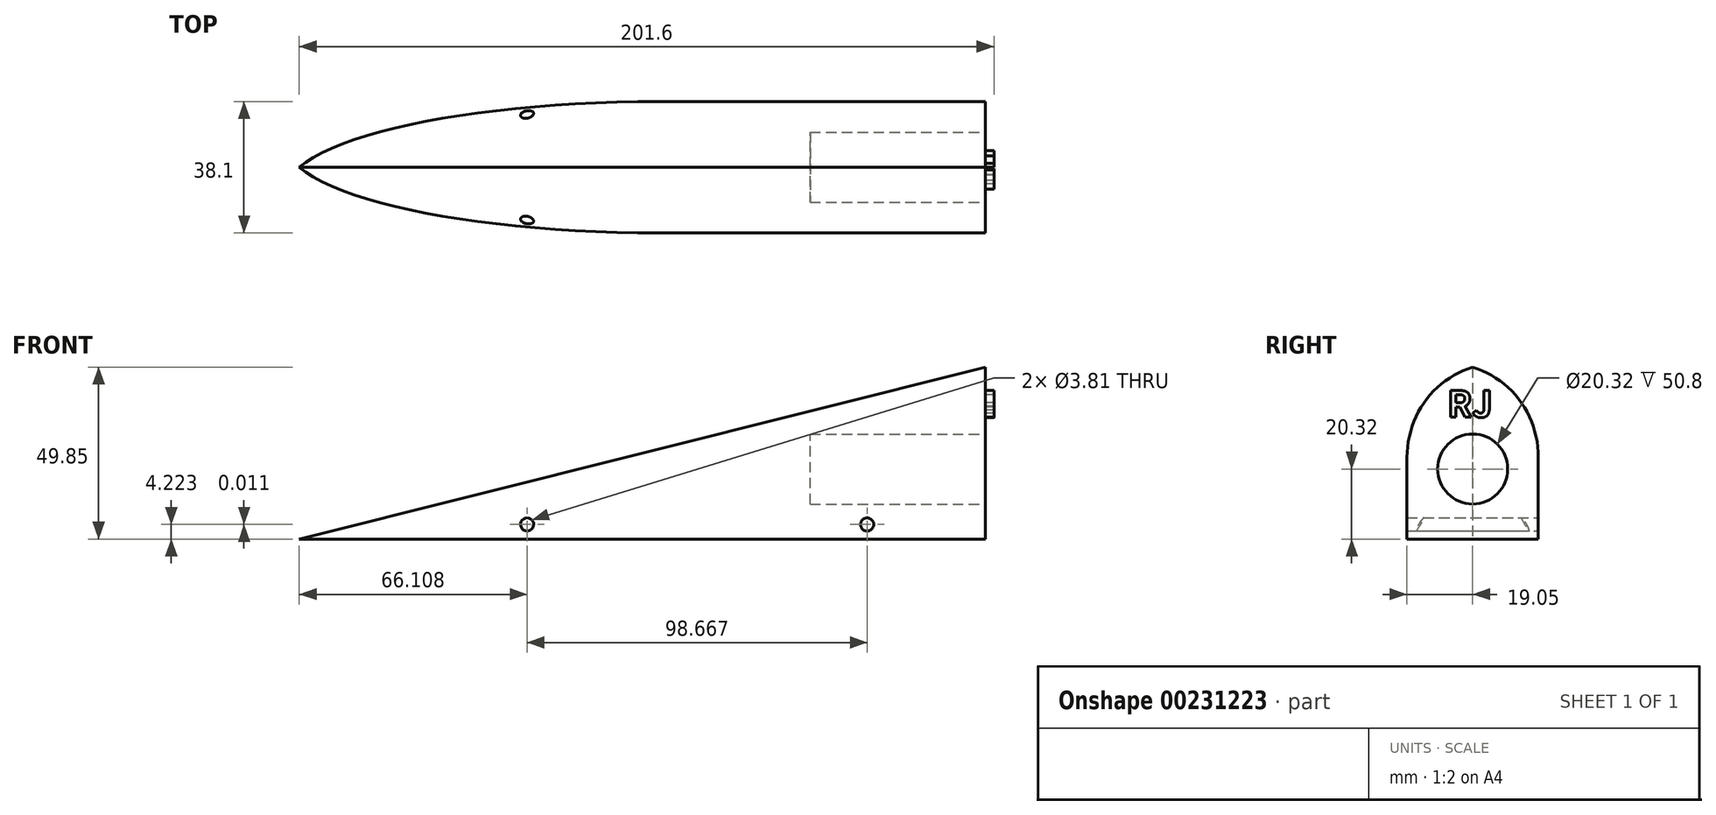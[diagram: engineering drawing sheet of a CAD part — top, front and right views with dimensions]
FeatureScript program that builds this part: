
annotation { "Feature Type Name" : "Feature", "Feature Type Description" : "" }
export const myFeature = defineFeature(function(context is Context, id is Id, definition is map)
    precondition{}
    {
        {
            var Q0;
            Q0=qCreatedBy(makeId("Front.planeOp"),FACE);
            var sketch = newSketch(context, id + "F0", { "sketchPlane" : qUnion([Q0])});
            skLineSegment(sketch, "E0", {"start": v(-100.5, 0) * mm, "end": v(102.82, 0) * mm});
            skLineSegment(sketch, "E1", {"start": v(102.82, 0) * mm, "end": v(102.82, 50.92) * mm});
            skLineSegment(sketch, "E2", {"start": v(-100.5, 0) * mm, "end": v(102.82, 50.92) * mm});
            skSolve(sketch);
        }
        {
            var Q0;
            Q0=makeQuery(id+"F0.imprint","IMPRINT",FACE,{"disambiguationData":[TD([[makeQuery(id+"F0.imprint","IMPRINT",EDGE,{"derivedFrom":sQuery(id+"F0.wireOp",EDGE,"E0")}),1.0]])]});
            extrude(context, id + "F1", {"entities" : qUnion([Q0]), "depth" : 38.1 * mm});
        }
        {
            var Q0;
            Q0=makeQuery(id+"F1.opExtrude","CAP_EDGE",EDGE,{"disambiguationData":[OSD([sQuery(id+"F0.wireOp",EDGE,"E2")])],"isStart":true});
            var Q1;
            Q1=makeQuery(id+"F1.opExtrude","CAP_EDGE",EDGE,{"disambiguationData":[OSD([sQuery(id+"F0.wireOp",EDGE,"E2")])],"isStart":false});
            fillet(context, id + "F2", {"entities" : qUnion([Q0, Q1]), "radius" : 26.37 * mm, "tangentPropagation" : true, "allowEdgeOverflow" : false});
        }
        {
            var Q0;
            Q0=makeQuery(id+"F1.opExtrude","SWEPT_FACE",FACE,{"disambiguationData":[OSD([sQuery(id+"F0.wireOp",EDGE,"E1")])]});
            var sketch = newSketch(context, id + "F3", { "sketchPlane" : qUnion([Q0])});
            skCircle(sketch, "E3", {"center": v(-19.05, 20.32) * mm, "radius": 10.16 * mm});
            skSolve(sketch);
        }
        {
            var Q0;
            Q0=makeQuery(id+"F3.imprint","IMPRINT",FACE,{"disambiguationData":[TD([[makeQuery(id+"F3.imprint","IMPRINT",EDGE,{"derivedFrom":sQuery(id+"F3.wireOp",EDGE,"E3")}),1.0]])]});
            extrude(context, id + "F4", {"entities" : qUnion([Q0]), "operationType" : NewBodyOperationType.REMOVE, "oppositeDirection" : true, "depth" : 50.8 * mm});
        }
        {
            var Q0;
            Q0=qCreatedBy(makeId("Front.planeOp"),FACE);
            var sketch = newSketch(context, id + "F5", { "sketchPlane" : qUnion([Q0])});
            skSolve(sketch);
        }
        {
            var Q0;
            Q0=makeQuery(id+"F1.opExtrude","CAP_FACE",FACE,{"disambiguationData":[OSD([sQuery(id+"F0.wireOp",EDGE,"E0"),sQuery(id+"F0.wireOp",EDGE,"E1"),sQuery(id+"F0.wireOp",EDGE,"E2")])],"isStart":true});
            var sketch = newSketch(context, id + "F6", { "sketchPlane" : qUnion([Q0])});
            skCircle(sketch, "E4", {"center": v(-68.54, 4.22) * mm, "radius": 1.9 * mm});
            skSolve(sketch);
        }
        {
            var Q0;
            Q0=makeQuery(id+"F6.imprint","IMPRINT",FACE,{"disambiguationData":[TD([[makeQuery(id+"F6.imprint","IMPRINT",EDGE,{"derivedFrom":sQuery(id+"F6.wireOp",EDGE,"E4")}),1.0]])]});
            var Q1;
            Q1=sQuery(id+"F6.wireOp",EDGE,"E4");
            extrude(context, id + "F7", {"entities" : qUnion([Q0]), "operationType" : NewBodyOperationType.REMOVE, "surfaceEntities" : qUnion([Q1]), "oppositeDirection" : true, "depth" : 50.8 * mm});
        }
        {
            var Q0;
            Q0=makeQuery(id+"F1.opExtrude","SWEPT_FACE",FACE,{"disambiguationData":[OSD([sQuery(id+"F0.wireOp",EDGE,"E1")])]});
            var sketch = newSketch(context, id + "F8", { "sketchPlane" : qUnion([Q0])});
            skText(sketch, "E5", { "text": "RJ", "fontName": "NotoSansCJKsc-Bold.otf"});
            const initialGuessF8  = {"E5": [-0.02641, 0.03535, 1, 0, 0.00756]};
            skSetInitialGuess(sketch, initialGuessF8);
            skSolve(sketch);
        }
        {
            var Q0;
            Q0 = qSketchRegion(id + "F5", true);
            var Q1;
            Q1 = qSketchRegion(id + "F8", true);
            extrude(context, id + "F9", {"entities" : qUnion([Q0, Q1]), "operationType" : NewBodyOperationType.ADD, "depth" : 2.54 * mm});
        }
        {
            var Q0;
            Q0=qCreatedBy(makeId("Front.planeOp"),FACE);
            var sketch = newSketch(context, id + "F10", { "sketchPlane" : qUnion([Q0])});
            skCircle(sketch, "E6", {"center": v(-30.13, 4.23) * mm, "radius": 1.9 * mm});
            skSolve(sketch);
        }
        {
            var Q0;
            Q0 = qSketchRegion(id + "F10", true);
            extrude(context, id + "F11", {"entities" : qUnion([Q0]), "operationType" : NewBodyOperationType.REMOVE, "depth" : 50.8 * mm});
        }
    });
